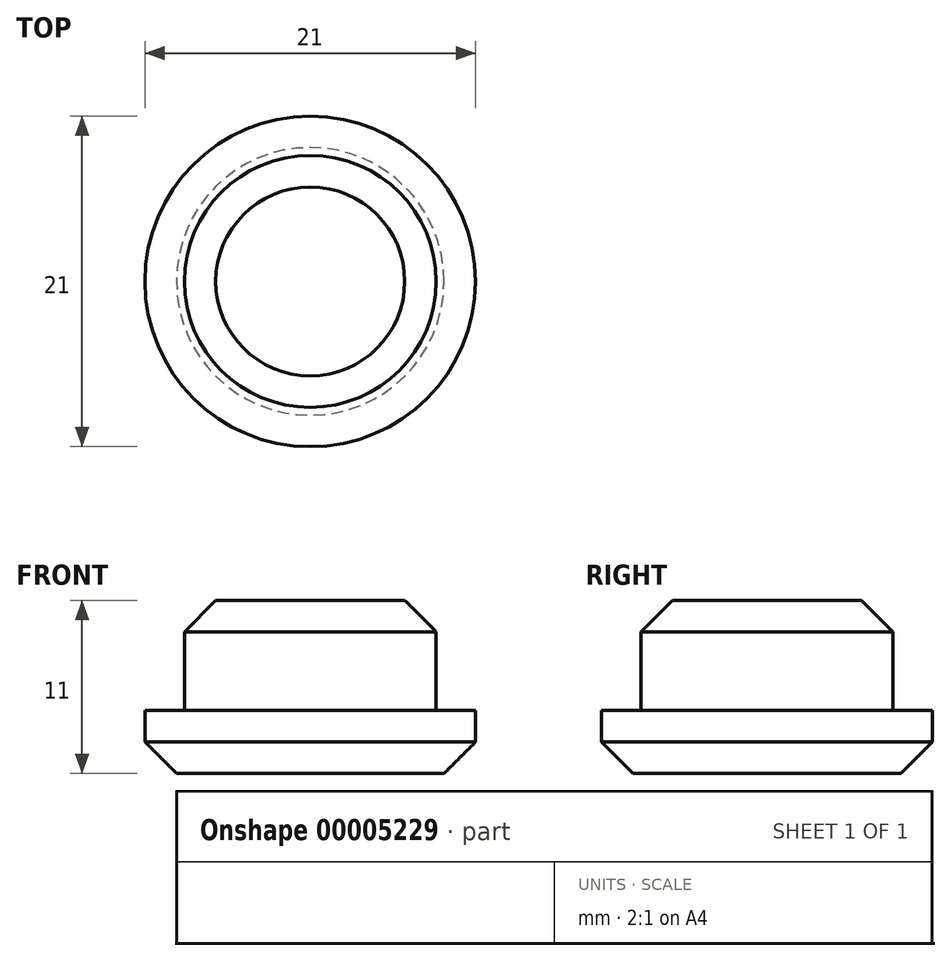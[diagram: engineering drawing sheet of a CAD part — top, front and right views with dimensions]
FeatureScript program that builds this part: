
annotation { "Feature Type Name" : "Feature", "Feature Type Description" : "" }
export const myFeature = defineFeature(function(context is Context, id is Id, definition is map)
    precondition{}
    {
        {
            var Q0;
            Q0=qCreatedBy(makeId("Top.planeOp"),FACE);
            var sketch = newSketch(context, id + "F0", { "sketchPlane" : qUnion([Q0])});
            skCircle(sketch, "E0", {"center": v(0, 0) * mm, "radius": 10.5 * mm});
            skSolve(sketch);
        }
        {
            var Q0;
            Q0=makeQuery(id+"F0.imprint","IMPRINT",FACE,{"disambiguationData":[TD([[makeQuery(id+"F0.imprint","IMPRINT",EDGE,{"derivedFrom":sQuery(id+"F0.wireOp",EDGE,"E0")}),1.0]])]});
            extrude(context, id + "F1", {"entities" : qUnion([Q0]), "depth" : 4 * mm});
        }
        {
            var Q0;
            Q0=makeQuery(id+"F1.opExtrude","CAP_FACE",FACE,{"disambiguationData":[OSD([sQuery(id+"F0.wireOp",EDGE,"E0")])],"isStart":false});
            var sketch = newSketch(context, id + "F2", { "sketchPlane" : qUnion([Q0])});
            skCircle(sketch, "E1", {"center": v(0, 0) * mm, "radius": 8 * mm});
            skSolve(sketch);
        }
        {
            var Q0;
            Q0=makeQuery(id+"F2.imprint","IMPRINT",FACE,{"disambiguationData":[TD([[makeQuery(id+"F2.imprint","IMPRINT",EDGE,{"derivedFrom":sQuery(id+"F2.wireOp",EDGE,"E1")}),1.0]])]});
            extrude(context, id + "F3", {"entities" : qUnion([Q0]), "operationType" : NewBodyOperationType.ADD, "depth" : 7 * mm});
        }
        {
            var Q0;
            Q0=makeQuery(id+"F3.opExtrude","CAP_EDGE",EDGE,{"disambiguationData":[OSD([sQuery(id+"F2.wireOp",EDGE,"E1")])],"isStart":false});
            var Q1;
            Q1=makeQuery(id+"F1.opExtrude","CAP_EDGE",EDGE,{"disambiguationData":[OSD([sQuery(id+"F0.wireOp",EDGE,"E0")])],"isStart":true});
            chamfer(context, id + "F4", {"entities" : qUnion([Q0, Q1]), "width" : 2 * mm, "tangentPropagation" : true});
        }
    });
